# Revit family: VL2xGPS200xSWxBx
name_source: partatom
category: Leuchten
units: mm (PartAtom-declared; Revit-internal decimal feet)

## family parameters
Basisbauteil = Fläche
Beim Laden mit Abzugskörper schneiden = Nein
Bemaßung runder Anschluss = Durchmesser verwenden
Gemeinsam genutzt = Nein
Lichtquelle = Ja
OmniClass-Nummer = 23.80.70.11
OmniClass-Titel = Luminaries for Internal Lighting
Raumberechnungspunkt = Nein
Teiletyp = Normal

## types (1)
- VL2P-GPS200-5FLSW840B1400
    Baugruppenkennzeichen = D5020200
    Datei für fotometrisches Netz = Master_VL1GP1486-5RFWS840B0900.IES
    Emissionsform beim Rendern sichtbar = Nein
    Farbfilter = 16777215
    Farbtemperaturverschiebung bei Dämpfen der Lampe = <Keine Auswahl>
    Hersteller = RIDI Leuchten GmbH
    Lampe = LED
    Modell = 2550044SW
    Neigungswinkel = 90.00°
    Scheinlast = 77 VA
    URL = www.ridi.de
    Von Breite des Rechtecks ausssenden = 1979 mm  [stored 6.49278 ft]
    Von Länge des Rechtecks aussenden = 61 mm  [stored 0.200131 ft]
    Vorgabe-Ansicht = 0 mm  [stored 0 ft]
    brand = RIDI
    conformity mark = CE
    electrical safety class = 1
    height = 64 mm  [stored 0.209974 ft]
    ingress protection (IP) code = IP54
    length = 2000 mm  [stored 6.56168 ft]
    nominal frequency = 50-60Hz
    nominal voltage = 230
    product name = VL2P-GPS200-5FLSW840B1400
    rated input power = 77
    voltage type (AC, DC, UC) = AC
    weight = 2,1kg
    width = 67 mm

note: [stored X ft] marks values corroborated as IEEE doubles in the binary element streams (Revit-internal decimal feet)
